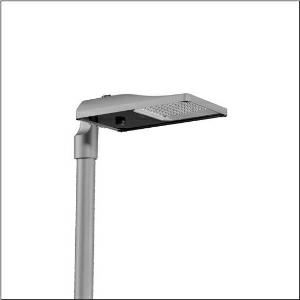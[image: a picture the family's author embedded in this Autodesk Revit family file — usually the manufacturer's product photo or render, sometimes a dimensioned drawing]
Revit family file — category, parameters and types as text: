
# Revit family: streetlight_sl_31_midi___st0_5a_5xh7b4at08la_3b68
name_source: partatom
category: Lighting Fixtures
units: mm (PartAtom-declared; Revit-internal decimal feet)

## family parameters
Cut with Voids When Loaded = No
Host = Face
Light Source = No
Part Type = Normal
Room Calculation Point = No
Round Connector Dimension = Use Diameter
Shared = No

## types (1)
- --- (1 x LED, 13610 lm, 86.5 W, 4000K)
    Apparent Load = 87 VA
    CIE Flux Codes = 41 75 97 100 100
    Color Rendering = 70
    Color Temperature = 4000K
    Default Elevation = 1800 mm
    Description = Streetlight SL 31 midi D4i mast luminaire for post-top, side-entry; light control with lens of PMMA; light distribution: ST0.5a, direct asymmetric distribution, for standard-compliant lighting for roads and squares; LED: luminous flux: 13.610lm, light colour: 740, colour temperature: 4000K; luminous efficacy: 157,3lm/W; control: pre-setting: logarithmic dimming characteristic, flexible luminous flux parameterisation, time-dependent luminous flux control, constant luminous flux control, power reduction, intelligent temperature release in ECG and LED module, overheat protection; luminaire housing, of diecast aluminium, SITECO metallic grey (DB 702S), corrosivity category C5 high according to DIN EN ISO 12944; cover of toughened safety glass, transparent, opened without tools; mast flange of diecast aluminium, SITECO metallic grey (DB 702S), spigot size: 76/60mm, mast flange included unmounted; cable length: 10,5m, connection cable pre-assembled; mains connection: 220..240V, AC, 50/60Hz; power consumption (at start of service life): 86,5W / (at end of service life): 90W / (with reduced operation 50%): 39,6W; protection rating (complete): IP66; insulation class (complete): insulation class II (safety insulation); impact resistance: IK09; certification: CE, ENEC, ENEC+, VDE, UKCA, ZD4i; permissible operating ambient temperature for outdoor applications: -40..+50°C; packaging unit: 1 piece

Light Distribution: ST0.5a
    Height = 79 mm
    Lamp = 1 x LED
    Lamp Light Flux = 13610 lm
    Lamp Power = 86.5 W
    Lamp count = 1
    Length = 577 mm
    Luminous efficacy = 157 lm/W
    Manufacturer = Siteco
    ModVariant = No
    Model = 5XH7B4AT08LA
    Number of Poles = 1
    OnlyDefault = Yes
    Power Factor = 1
    Product Name = Streetlight SL 31 midi | ST0.5a
    Product group = mast luminaire | pylon top
    ProductGroupID = 6100
    Protection Class = Protection class II
    Protection Degree = IP 66
    RLX_Detail_Level = 1
    RLX_Emergency_Light_Flux = 0 lm
    RLX_Emergency_Type = 0
    RLX_Emergency_Type_DB = No
    RlxData = <blob elided: 53537 chars, md5=89e753ec>
    Socket = socket
    Standby Power = 0 W
    System Light Flux = 13610 lm
    System Power = 87 W
    Type Comments = factory setting: luminous flux: 100 % | dim-lin: 254 | 456 mA
    Type Image = l_1300321.jpg
    URL = http://relux.com
    VarID = @adj_064427
    Voltage = 0 V
    Weight = 0.00 kg
    Width = 362 mm

## geometry (parser evidence)
native form markers: Blend x4, Sweep x11
no freeform markers — native parametric forms only
